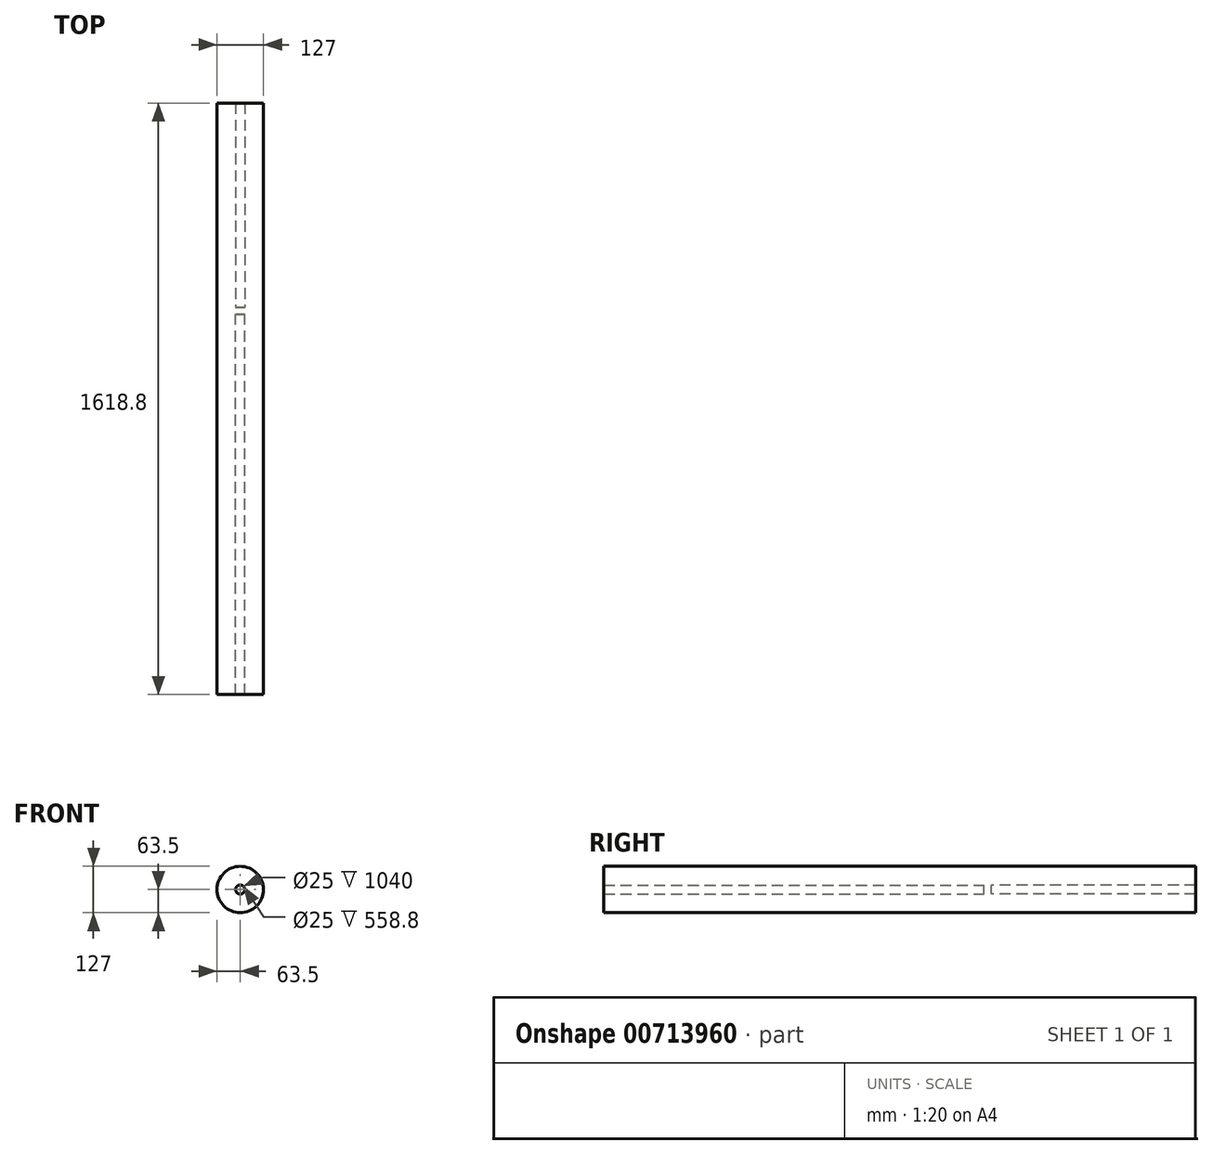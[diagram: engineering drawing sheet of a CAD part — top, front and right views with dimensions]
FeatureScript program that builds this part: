
annotation { "Feature Type Name" : "Feature", "Feature Type Description" : "" }
export const myFeature = defineFeature(function(context is Context, id is Id, definition is map)
    precondition{}
    {
        {
            var Q0;
            Q0=qCreatedBy(makeId("Front.planeOp"),FACE);
            var sketch = newSketch(context, id + "F0", { "sketchPlane" : qUnion([Q0])});
            skCircle(sketch, "E0", {"center": v(0, 0) * mm, "radius": 12.5 * mm});
            skCircle(sketch, "E1", {"center": v(0, 0) * mm, "radius": 63.5 * mm});
            skSolve(sketch);
        }
        {
            var Q0;
            Q0=makeQuery(id+"F0.imprint","IMPRINT",FACE,{"disambiguationData":[TD([[makeQuery(id+"F0.imprint","IMPRINT",EDGE,{"derivedFrom":sQuery(id+"F0.wireOp",EDGE,"E1")}),1.0]])]});
            var Q1;
            Q1=makeQuery(id+"F0.imprint","IMPRINT",FACE,{"disambiguationData":[TD([[makeQuery(id+"F0.imprint","IMPRINT",EDGE,{"derivedFrom":sQuery(id+"F0.wireOp",EDGE,"E0")}),1.0]])]});
            extrude(context, id + "F1", {"entities" : qUnion([Q0, Q1]), "depth" : 20 * mm, "offsetDistance" : 25.4 * mm});
        }
        {
            var Q0;
            Q0=makeQuery(id+"F0.imprint","IMPRINT",FACE,{"disambiguationData":[TD([[makeQuery(id+"F0.imprint","IMPRINT",EDGE,{"derivedFrom":sQuery(id+"F0.wireOp",EDGE,"E1")}),1.0]])]});
            extrude(context, id + "F2", {"entities" : qUnion([Q0]), "operationType" : NewBodyOperationType.ADD, "depth" : 1060 * mm, "offsetDistance" : 25.4 * mm});
        }
        {
            var Q0;
            Q0=makeQuery(id+"F0.imprint","IMPRINT",FACE,{"disambiguationData":[TD([[makeQuery(id+"F0.imprint","IMPRINT",EDGE,{"derivedFrom":sQuery(id+"F0.wireOp",EDGE,"E1")}),1.0]])]});
            var Q1;
            Q1=makeQuery(id+"F2.opExtrude","CAP_FACE",FACE,{"disambiguationData":[OSD([sQuery(id+"F0.wireOp",EDGE,"E1")])],"isStart":false});
            extrude(context, id + "F3", {"entities" : qUnion([Q0, Q1]), "operationType" : NewBodyOperationType.ADD, "oppositeDirection" : true, "depth" : 558.8 * mm, "offsetDistance" : 25.4 * mm});
        }
    });
